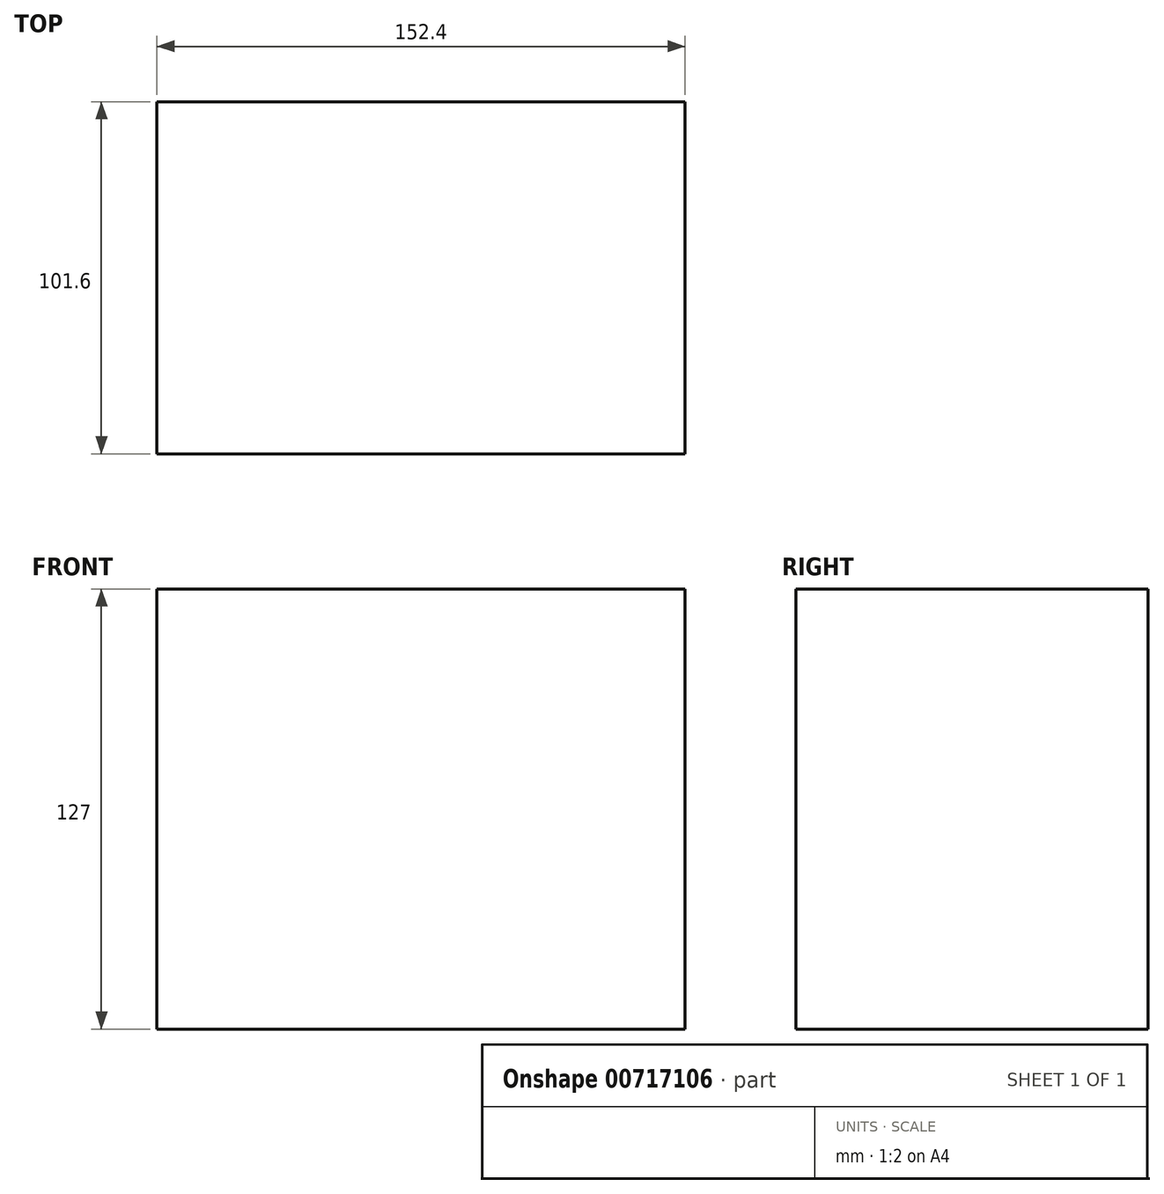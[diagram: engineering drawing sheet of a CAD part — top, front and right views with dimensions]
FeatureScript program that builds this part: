
annotation { "Feature Type Name" : "Feature", "Feature Type Description" : "" }
export const myFeature = defineFeature(function(context is Context, id is Id, definition is map)
    precondition{}
    {
        {
            var Q0;
            Q0=qCreatedBy(makeId("Front.planeOp"),FACE);
            var sketch = newSketch(context, id + "F0", { "sketchPlane" : qUnion([Q0])});
            skLineSegment(sketch, "E0", {"start": v(-118.54, 58.13) * mm, "end": v(-118.54, -68.87) * mm});
            skLineSegment(sketch, "E1", {"start": v(-118.54, -68.87) * mm, "end": v(33.86, -68.87) * mm});
            skLineSegment(sketch, "E2", {"start": v(33.86, -68.87) * mm, "end": v(33.86, 58.13) * mm});
            skLineSegment(sketch, "E3", {"start": v(33.86, 58.13) * mm, "end": v(-118.54, 58.13) * mm});
            skSolve(sketch);
        }
        {
            var Q0;
            Q0=makeQuery(id+"F0.imprint","IMPRINT",FACE,{"disambiguationData":[TD([[makeQuery(id+"F0.imprint","IMPRINT",EDGE,{"derivedFrom":sQuery(id+"F0.wireOp",EDGE,"E0")}),1.0]])]});
            extrude(context, id + "F1", {"entities" : qUnion([Q0]), "depth" : 101.6 * mm, "offsetDistance" : 25.4 * mm});
        }
    });
